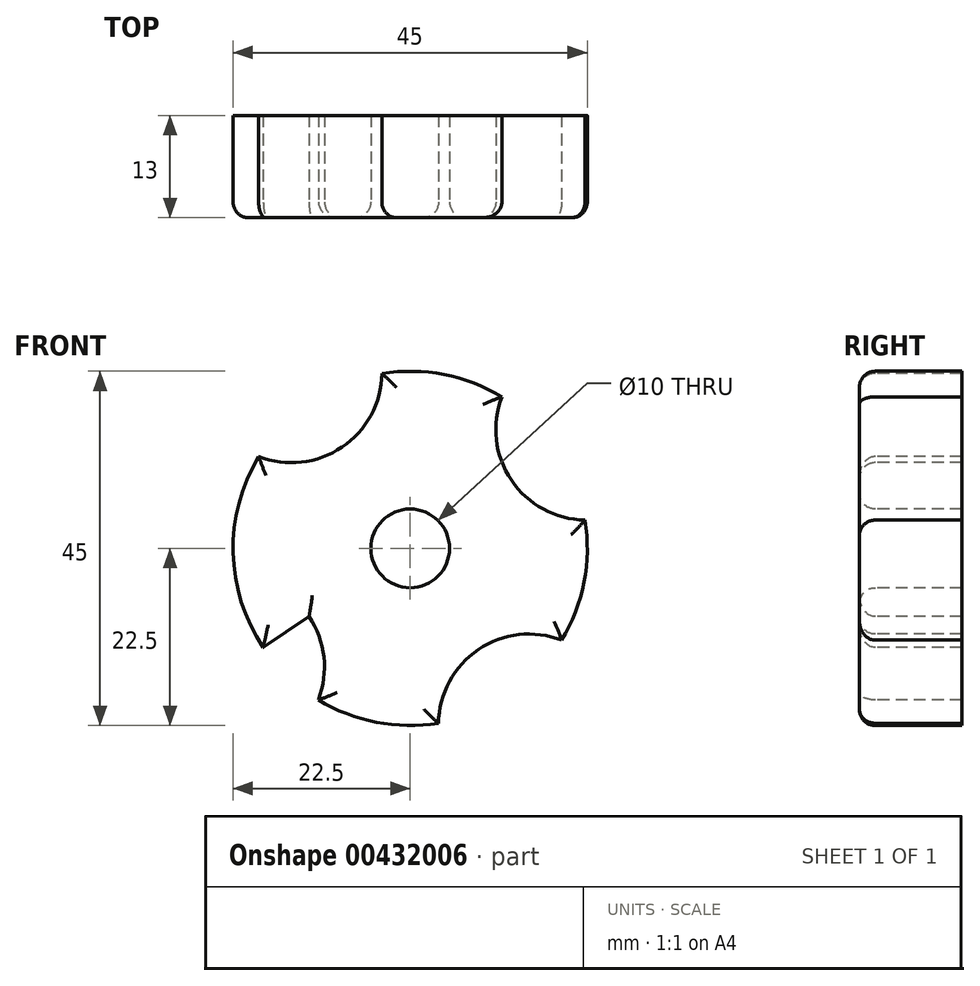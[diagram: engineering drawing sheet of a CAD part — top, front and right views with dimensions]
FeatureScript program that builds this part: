
annotation { "Feature Type Name" : "Feature", "Feature Type Description" : "" }
export const myFeature = defineFeature(function(context is Context, id is Id, definition is map)
    precondition{}
    {
        {
            var Q0;
            Q0=qCreatedBy(makeId("Front.planeOp"),FACE);
            var sketch = newSketch(context, id + "F0", { "sketchPlane" : qUnion([Q0])});
            skCircle(sketch, "E0", {"center": v(0, 0) * mm, "radius": 22.5 * mm});
            skSolve(sketch);
        }
        {
            var Q0;
            Q0=makeQuery(id+"F0.imprint","IMPRINT",FACE,{"disambiguationData":[TD([[makeQuery(id+"F0.imprint","IMPRINT",EDGE,{"derivedFrom":sQuery(id+"F0.wireOp",EDGE,"E0")}),1.0]])]});
            extrude(context, id + "F1", {"entities" : qUnion([Q0]), "depth" : 13 * mm});
        }
        {
            var Q0;
            Q0=makeQuery(id+"F1.opExtrude","CAP_FACE",FACE,{"disambiguationData":[OSD([sQuery(id+"F0.wireOp",EDGE,"E0")])],"isStart":false});
            var sketch = newSketch(context, id + "F2", { "sketchPlane" : qUnion([Q0])});
            skLineSegment(sketch, "E1", {"start": v(0, 0) * mm, "end": v(22.5, 0) * mm, "construction": true});
            skLineSegment(sketch, "E2", {"start": v(0, 0) * mm, "end": v(0, 22.5) * mm, "construction": true});
            skCircle(sketch, "E3", {"center": v(0, 0) * mm, "radius": 5 * mm});
            skSolve(sketch);
        }
        {
            var Q0;
            Q0=sQuery(id+"F2.wireOp",VERTEX,"E3.center");
            var Q1;
            Q1=makeQuery(id+"F1.opExtrude","SWEPT_BODY",BODY,{"disambiguationData":[OSD([sQuery(id+"F0.wireOp",EDGE,"E0")])]});
            hole(context, id + "F3", {"style" : HoleStyle.SIMPLE, "endStyle" : HoleEndStyle.THROUGH, "holeDiameter" : 10 * mm, "isTappedThrough" : true, "tappedDepth" : 12 * mm, "tapClearance" : 3, "locations" : qUnion([Q0]), "scope" : qUnion([Q1])});
        }
        {
            var Q0;
            Q0=makeQuery(id+"F1.opExtrude","CAP_FACE",FACE,{"disambiguationData":[OSD([sQuery(id+"F0.wireOp",EDGE,"E0")])],"isStart":false});
            var sketch = newSketch(context, id + "F4", { "sketchPlane" : qUnion([Q0])});
            skCircle(sketch, "E4", {"center": v(-22.38, -15.1) * mm, "radius": 11.5 * mm});
            skLineSegment(sketch, "E5", {"start": v(0, 0) * mm, "end": v(-22.5, 0) * mm, "construction": true});
            skLineSegment(sketch, "E6", {"start": v(0, 0) * mm, "end": v(-22.38, -15.1) * mm});
            skCircle(sketch, "E7.1.0", {"center": v(15.1, -22.38) * mm, "radius": 11.5 * mm});
            skCircle(sketch, "E7.2.0", {"center": v(22.38, 15.1) * mm, "radius": 11.5 * mm});
            skCircle(sketch, "E7.3.0", {"center": v(-15.1, 22.38) * mm, "radius": 11.5 * mm});
            skPoint(sketch, "E7.center", {"position": v(0, 0) * mm});
            skSolve(sketch);
        }
        {
            var Q0;
            {var subQ0=sQuery(id+"F4.wireOp",EDGE,"E4");var subQ1=makeQuery(id+"F1.opExtrude","CAP_EDGE",EDGE,{"disambiguationData":[OSD([sQuery(id+"F0.wireOp",EDGE,"E0")])],"isStart":false});var subQ2=makeQuery(id+"F4.imprint","INTERSECT",VERTEX,{"disambiguationData":[OD(0.0)],"derivedFrom":[subQ1,subQ0]});Q0=makeQuery(id+"F4.imprint","IMPRINT",FACE,{"disambiguationData":[TD([[makeQuery(id+"F4.imprint","IMPRINT",EDGE,{"disambiguationData":[TD([[subQ2,1.0]])],"derivedFrom":subQ0}),1.0]])]});}
            var Q1;
            {var subQ0=sQuery(id+"F4.wireOp",EDGE,"E6");var subQ1=sQuery(id+"F4.wireOp",EDGE,"E4");var subQ2=makeQuery(id+"F4.imprint","INTERSECT",VERTEX,{"derivedFrom":[subQ1,subQ0]});Q1=makeQuery(id+"F4.imprint","IMPRINT",FACE,{"disambiguationData":[TD([[makeQuery(id+"F4.imprint","IMPRINT",EDGE,{"disambiguationData":[TD([[subQ2,1.0]])],"derivedFrom":subQ1}),1.0]])]});}
            var Q2;
            {var subQ0=sQuery(id+"F4.wireOp",EDGE,"E7.1.0");var subQ1=makeQuery(id+"F1.opExtrude","CAP_EDGE",EDGE,{"disambiguationData":[OSD([sQuery(id+"F0.wireOp",EDGE,"E0")])],"isStart":false});var subQ2=makeQuery(id+"F4.imprint","INTERSECT",VERTEX,{"disambiguationData":[OD(0.0)],"derivedFrom":[subQ1,subQ0]});Q2=makeQuery(id+"F4.imprint","IMPRINT",FACE,{"disambiguationData":[TD([[makeQuery(id+"F4.imprint","IMPRINT",EDGE,{"disambiguationData":[TD([[subQ2,1.0]])],"derivedFrom":subQ0}),1.0]])]});}
            var Q3;
            {var subQ0=sQuery(id+"F4.wireOp",EDGE,"E7.2.0");var subQ1=makeQuery(id+"F1.opExtrude","CAP_EDGE",EDGE,{"disambiguationData":[OSD([sQuery(id+"F0.wireOp",EDGE,"E0")])],"isStart":false});var subQ2=makeQuery(id+"F4.imprint","INTERSECT",VERTEX,{"disambiguationData":[OD(0.0)],"derivedFrom":[subQ1,subQ0]});Q3=makeQuery(id+"F4.imprint","IMPRINT",FACE,{"disambiguationData":[TD([[makeQuery(id+"F4.imprint","IMPRINT",EDGE,{"disambiguationData":[TD([[subQ2,1.0]])],"derivedFrom":subQ0}),1.0]])]});}
            var Q4;
            {var subQ0=sQuery(id+"F4.wireOp",EDGE,"E7.3.0");var subQ1=makeQuery(id+"F1.opExtrude","CAP_EDGE",EDGE,{"disambiguationData":[OSD([sQuery(id+"F0.wireOp",EDGE,"E0")])],"isStart":false});var subQ2=makeQuery(id+"F4.imprint","INTERSECT",VERTEX,{"disambiguationData":[OD(0.0)],"derivedFrom":[subQ1,subQ0]});Q4=makeQuery(id+"F4.imprint","IMPRINT",FACE,{"disambiguationData":[TD([[makeQuery(id+"F4.imprint","IMPRINT",EDGE,{"disambiguationData":[TD([[subQ2,-1.0]])],"derivedFrom":subQ0}),1.0]])]});}
            extrude(context, id + "F5", {"entities" : qUnion([Q0, Q1, Q2, Q3, Q4]), "operationType" : NewBodyOperationType.REMOVE, "oppositeDirection" : true, "depth" : 25 * mm});
        }
        {
            var Q0;
            Q0=makeQuery(id+"F1.opExtrude","CAP_FACE",FACE,{"disambiguationData":[OSD([sQuery(id+"F0.wireOp",EDGE,"E0")])],"isStart":false});
            fillet(context, id + "F6", {"entities" : qUnion([Q0]), "radius" : 2 * mm, "tangentPropagation" : true, "allowEdgeOverflow" : false});
        }
    });
